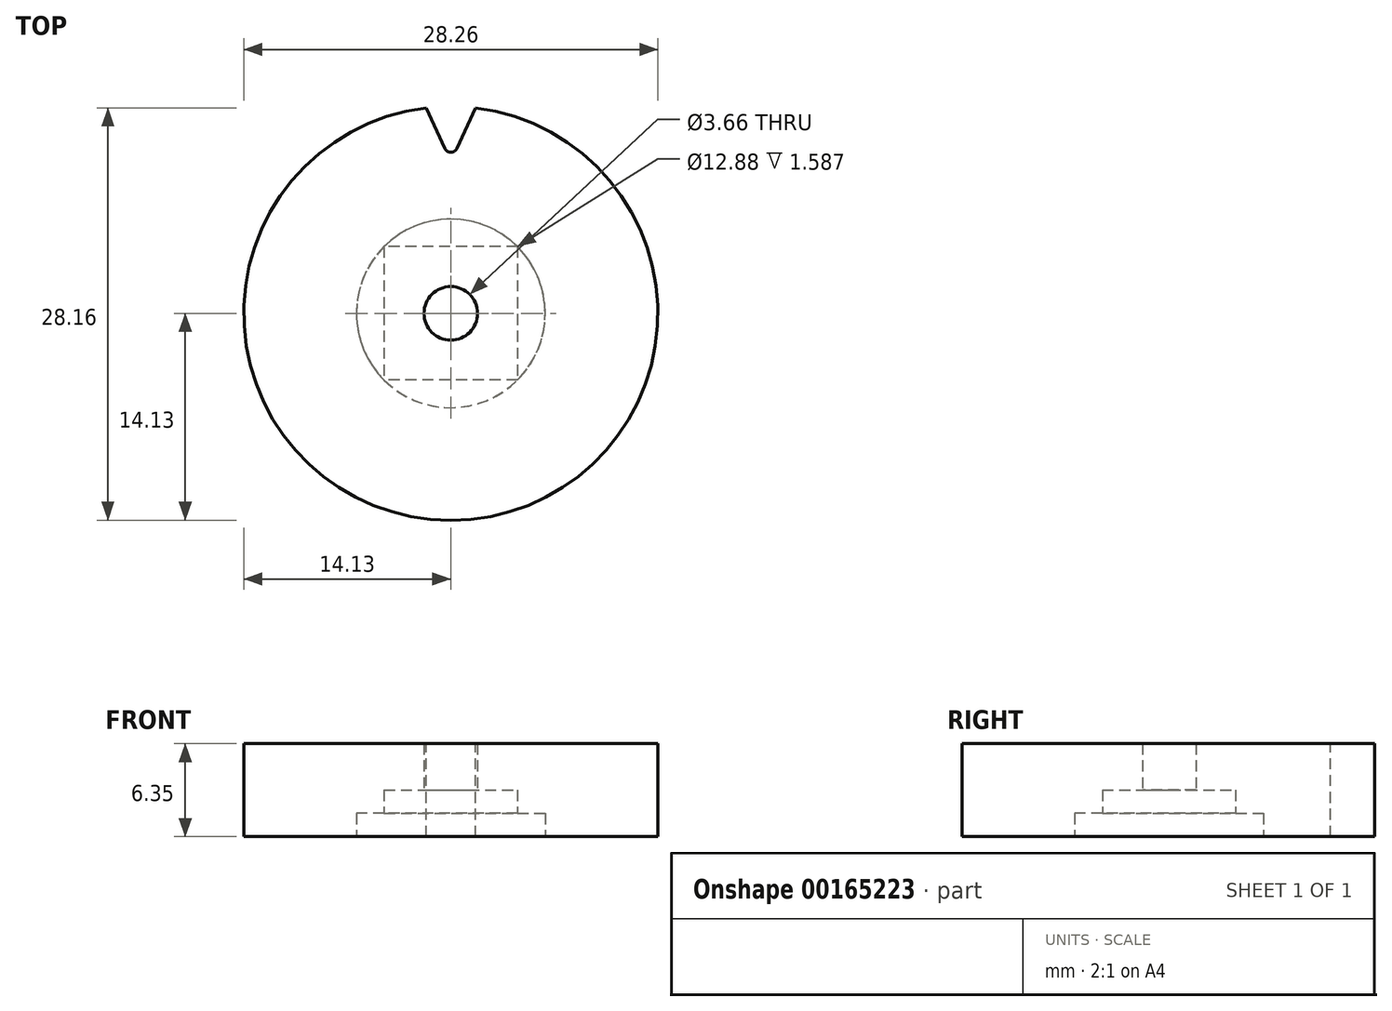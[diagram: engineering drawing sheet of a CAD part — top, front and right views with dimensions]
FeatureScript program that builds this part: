
annotation { "Feature Type Name" : "Feature", "Feature Type Description" : "" }
export const myFeature = defineFeature(function(context is Context, id is Id, definition is map)
    precondition{}
    {
        {
            var Q0;
            Q0=qCreatedBy(makeId("Top.planeOp"),FACE);
            var sketch = newSketch(context, id + "F0", { "sketchPlane" : qUnion([Q0])});
            skCircle(sketch, "E0", {"center": v(0, 0) * mm, "radius": 14.13 * mm});
            skCircle(sketch, "E1", {"center": v(0, 0) * mm, "radius": 1.83 * mm});
            skSolve(sketch);
        }
        {
            var Q0;
            Q0 = qSketchRegion(id + "F0", true);
            extrude(context, id + "F1", {"entities" : qUnion([Q0]), "depth" : 6.35 * mm});
        }
        {
            var Q0;
            Q0=makeQuery(id+"F1.opExtrude","CAP_FACE",FACE,{"disambiguationData":[OSD([sQuery(id+"F0.wireOp",EDGE,"E0"),sQuery(id+"F0.wireOp",EDGE,"E1")])],"isStart":true});
            var sketch = newSketch(context, id + "F2", { "sketchPlane" : qUnion([Q0])});
            skLineSegment(sketch, "E2.bottom", {"start": v(-4.55, 4.55) * mm, "end": v(4.55, 4.55) * mm});
            skLineSegment(sketch, "E2.top", {"start": v(-4.55, -4.55) * mm, "end": v(4.55, -4.55) * mm});
            skLineSegment(sketch, "E2.left", {"start": v(-4.55, 4.55) * mm, "end": v(-4.55, -4.55) * mm});
            skLineSegment(sketch, "E2.right", {"start": v(4.55, 4.55) * mm, "end": v(4.55, -4.55) * mm});
            skPoint(sketch, "E2.middle", {"position": v(0, 0) * mm});
            skCircle(sketch, "E3", {"center": v(0, 0) * mm, "radius": 6.44 * mm, "construction": true});
            skSolve(sketch);
        }
        {
            var Q0;
            Q0 = qSketchRegion(id + "F2", true);
            extrude(context, id + "F3", {"entities" : qUnion([Q0]), "operationType" : NewBodyOperationType.REMOVE, "oppositeDirection" : true, "depth" : 3.17 * mm});
        }
        {
            var Q0;
            Q0=makeQuery(id+"F1.opExtrude","CAP_FACE",FACE,{"disambiguationData":[OSD([sQuery(id+"F0.wireOp",EDGE,"E0"),sQuery(id+"F0.wireOp",EDGE,"E1")])],"isStart":true});
            var sketch = newSketch(context, id + "F4", { "sketchPlane" : qUnion([Q0])});
            skCircle(sketch, "E4", {"center": v(0, 0) * mm, "radius": 6.44 * mm});
            skSolve(sketch);
        }
        {
            var Q0;
            Q0 = qSketchRegion(id + "F4", true);
            extrude(context, id + "F5", {"entities" : qUnion([Q0]), "operationType" : NewBodyOperationType.REMOVE, "oppositeDirection" : true, "depth" : 1.59 * mm});
        }
        {
            var Q0;
            Q0=makeQuery(id+"F1.opExtrude","CAP_FACE",FACE,{"disambiguationData":[OSD([sQuery(id+"F0.wireOp",EDGE,"E0"),sQuery(id+"F0.wireOp",EDGE,"E1")])],"isStart":false});
            var sketch = newSketch(context, id + "F6", { "sketchPlane" : qUnion([Q0])});
            skLineSegment(sketch, "E5", {"start": v(0, 0) * mm, "end": v(0, 14.13) * mm, "construction": true});
            skLineSegment(sketch, "E6", {"start": v(0, 0) * mm, "end": v(1.16, 14.09) * mm, "construction": true});
            skArc(sketch, "E7", {"start": v(1.68, 14.03) * mm, "mid": v(0, 14.13) * mm, "end": v(-1.68, 14.03) * mm});
            skLineSegment(sketch, "E8", {"start": v(-1.68, 14.03) * mm, "end": v(-0.4, 11.26) * mm});
            skLineSegment(sketch, "E9", {"start": v(1.68, 14.03) * mm, "end": v(0.4, 11.26) * mm});
            skArc(sketch, "E10", {"start": v(-0.4, 11.26) * mm, "mid": v(0, 11) * mm, "end": v(0.4, 11.26) * mm});
            skPoint(sketch, "E11", {"position": v(1.04, 12.65) * mm});
            skSolve(sketch);
        }
        {
            var Q0;
            Q0 = qSketchRegion(id + "F6", true);
            var Q1;
            Q1=makeQuery(id+"F1.opExtrude","CAP_FACE",FACE,{"disambiguationData":[OSD([sQuery(id+"F0.wireOp",EDGE,"E0"),sQuery(id+"F0.wireOp",EDGE,"E1")])],"isStart":true});
            extrude(context, id + "F7", {"entities" : qUnion([Q0]), "operationType" : NewBodyOperationType.REMOVE, "endBound" : BoundingType.UP_TO_SURFACE, "oppositeDirection" : true, "endBoundEntityFace" : qUnion([Q1]), "depth" : 25.4 * mm});
        }
    });
